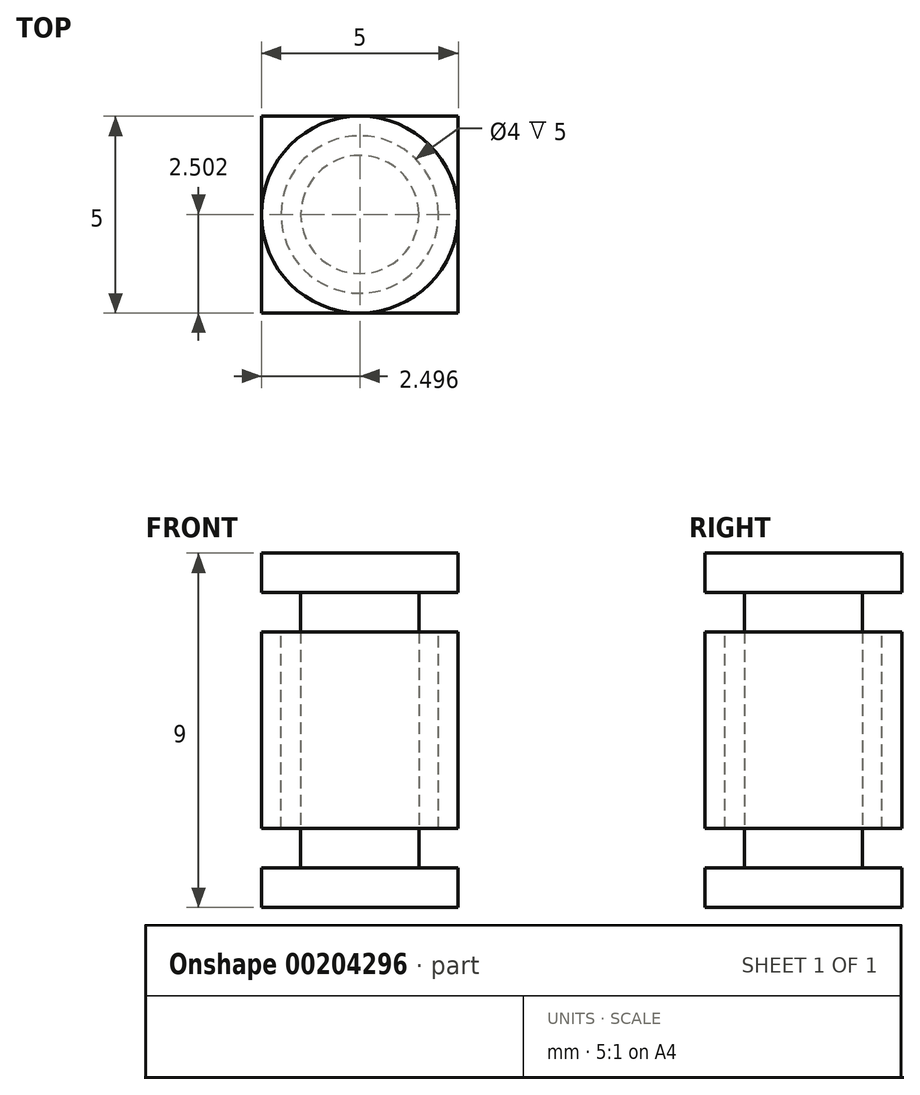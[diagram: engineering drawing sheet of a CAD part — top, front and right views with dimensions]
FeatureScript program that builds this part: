
annotation { "Feature Type Name" : "Feature", "Feature Type Description" : "" }
export const myFeature = defineFeature(function(context is Context, id is Id, definition is map)
    precondition{}
    {
        {
            var Q0;
            Q0=qCreatedBy(makeId("Top.planeOp"),FACE);
            var sketch = newSketch(context, id + "F0", { "sketchPlane" : qUnion([Q0])});
            skLineSegment(sketch, "E0.bottom", {"start": v(-60.61, 14.3) * mm, "end": v(-55.61, 14.3) * mm});
            skLineSegment(sketch, "E0.top", {"start": v(-60.61, 9.3) * mm, "end": v(-55.61, 9.3) * mm});
            skLineSegment(sketch, "E0.left", {"start": v(-60.61, 14.3) * mm, "end": v(-60.61, 9.3) * mm});
            skLineSegment(sketch, "E0.right", {"start": v(-55.61, 14.3) * mm, "end": v(-55.61, 9.3) * mm});
            skSolve(sketch);
        }
        {
            var Q0;
            Q0=makeQuery(id+"F0.imprint","IMPRINT",FACE,{"disambiguationData":[TD([[makeQuery(id+"F0.imprint","IMPRINT",EDGE,{"derivedFrom":sQuery(id+"F0.wireOp",EDGE,"E0.bottom")}),-1.0]])]});
            extrude(context, id + "F1", {"entities" : qUnion([Q0]), "depth" : 5 * mm});
        }
        {
            var Q0;
            Q0=makeQuery(id+"F1.opExtrude","CAP_FACE",FACE,{"disambiguationData":[OSD([sQuery(id+"F0.wireOp",EDGE,"E0.bottom"),sQuery(id+"F0.wireOp",EDGE,"E0.top"),sQuery(id+"F0.wireOp",EDGE,"E0.left"),sQuery(id+"F0.wireOp",EDGE,"E0.right")])],"isStart":false});
            var sketch = newSketch(context, id + "F2", { "sketchPlane" : qUnion([Q0])});
            skLineSegment(sketch, "E1", {"start": v(-55.61, 14.3) * mm, "end": v(-60.61, 9.3) * mm, "construction": true});
            skLineSegment(sketch, "E2", {"start": v(-60.61, 9.3) * mm, "end": v(-60.61, 14.3) * mm, "construction": true});
            skLineSegment(sketch, "E3", {"start": v(-60.61, 14.3) * mm, "end": v(-55.61, 9.3) * mm, "construction": true});
            skCircle(sketch, "E4", {"center": v(-58.11, 11.8) * mm, "radius": 2 * mm});
            skSolve(sketch);
        }
        {
            var Q0;
            Q0=makeQuery(id+"F2.imprint","IMPRINT",FACE,{"disambiguationData":[TD([[makeQuery(id+"F2.imprint","IMPRINT",EDGE,{"derivedFrom":sQuery(id+"F2.wireOp",EDGE,"E4")}),1.0]])]});
            extrude(context, id + "F3", {"entities" : qUnion([Q0]), "operationType" : NewBodyOperationType.REMOVE, "oppositeDirection" : true, "depth" : 25 * mm});
        }
        {
            var Q0;
            Q0=qCreatedBy(makeId("Top.planeOp"),FACE);
            var sketch = newSketch(context, id + "F4", { "sketchPlane" : qUnion([Q0])});
            skCircle(sketch, "E5", {"center": v(-58.11, 11.8) * mm, "radius": 1.5 * mm});
            skSolve(sketch);
        }
        {
            var Q0;
            Q0 = qSketchRegion(id + "F4", true);
            extrude(context, id + "F5", {"entities" : qUnion([Q0]), "depth" : 6 * mm});
        }
        {
            var Q0;
            Q0 = qSketchRegion(id + "F4", true);
            extrude(context, id + "F6", {"entities" : qUnion([Q0]), "operationType" : NewBodyOperationType.ADD, "oppositeDirection" : true, "depth" : 1 * mm});
        }
        {
            var Q0;
            Q0=makeQuery(id+"F5.opExtrude","CAP_FACE",FACE,{"disambiguationData":[OSD([sQuery(id+"F4.wireOp",EDGE,"E5")])],"isStart":false});
            var sketch = newSketch(context, id + "F7", { "sketchPlane" : qUnion([Q0])});
            skCircle(sketch, "E6", {"center": v(-58.11, 11.8) * mm, "radius": 2.5 * mm});
            skSolve(sketch);
        }
        {
            var Q0;
            Q0 = qSketchRegion(id + "F7", true);
            extrude(context, id + "F8", {"entities" : qUnion([Q0]), "operationType" : NewBodyOperationType.ADD, "depth" : 1 * mm});
        }
        {
            var Q0;
            Q0=makeQuery(id+"F6.opExtrude","CAP_FACE",FACE,{"disambiguationData":[OSD([sQuery(id+"F4.wireOp",EDGE,"E5")])],"isStart":false});
            var sketch = newSketch(context, id + "F9", { "sketchPlane" : qUnion([Q0])});
            skCircle(sketch, "E7", {"center": v(-58.11, -11.8) * mm, "radius": 2.5 * mm});
            skSolve(sketch);
        }
        {
            var Q0;
            Q0 = qSketchRegion(id + "F9", true);
            extrude(context, id + "F10", {"entities" : qUnion([Q0]), "operationType" : NewBodyOperationType.ADD, "depth" : 1 * mm});
        }
    });
